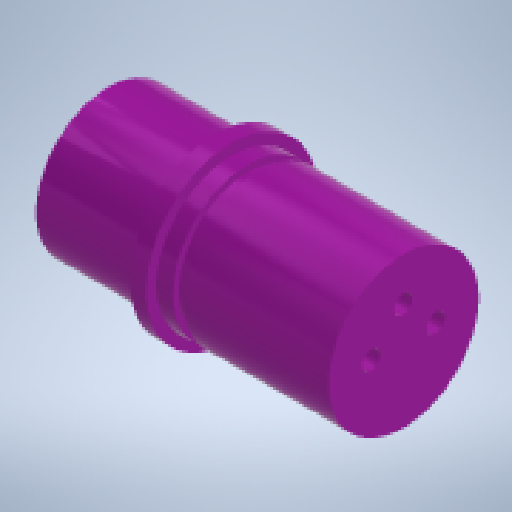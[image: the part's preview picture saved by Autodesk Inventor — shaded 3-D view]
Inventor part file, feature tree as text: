
AUTODESK INVENTOR PART (.ipt)
format: ipt  version: 2023 (Build 270158000, 158)  size: 334,336 bytes
history: native  units: mm
features: sketch x3, revolve x1, hole x1, extrude x1, projected_geometry x1
ambient origin geometry x8: Origin, YZ Plane, XZ Plane, XY Plane, X Axis, Y Axis, Z Axis, Center Point
bodies: Solid1 (feature_tree)
feature tree (7):
  revolve  "Revolution1"  [1 undecoded]
  hole  "Hole1"  [1 undecoded]
  extrude  "Extrusion1"  Depth=10.0mm
  sketch  "Sketch1"  dims[d0=28.0mm d1=32.0mm]
  sketch  "Sketch2"  dims[d2=3.0mm d3=35.0mm]
  sketch  "Sketch3"  dims[d4=360.0deg d5=10.0mm d6=5.0mm d7=3.0mm d10=3.4mm d11=4.0mm d12=6.3mm d13=2.0mm d14=90.0deg d15=4.5mm d16=20.594885mm d18=2.0mm d20=22.0mm d21=3.0mm d22=6.0mm d23=6.0mm d24=1.2mm d25=50.0mm d26=2.5mm d27=6.0mm d28=7.5mm d29=7.5mm d30=7.5mm d31=10.0mm d32=0.0mm]
  projected_geometry  "Projected Loop1"
note: 2 required parameter values undecoded (feature->parameter linkage not recoverable at this tier; creation-order binding heuristic only, values carry confidence <= 0.55)